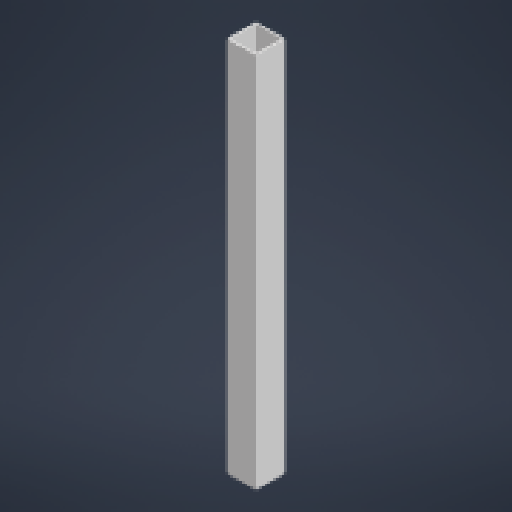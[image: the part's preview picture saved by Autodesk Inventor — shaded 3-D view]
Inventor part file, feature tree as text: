
AUTODESK INVENTOR PART (.ipt)
format: ipt  version: 2024 (Build 280153000, 153)  size: 129,536 bytes
history: native  units: in
note: dims shown in document units (in); Inventor stores cm internally (conversion verified against a paired STEP export)
features: plane x1, extrude x1, sketch x1
ambient origin geometry x8: Origin, YZ Plane, XZ Plane, XY Plane, X Axis, Y Axis, Z Axis, Center Point
bodies: Solid1 (feature_tree)
feature tree (3):
  plane  "Work Plane1"
  extrude  "Extrusion1"  Depth=1.0in
  sketch  "Sketch1"  dims[d0=1.0in d1=1.0in d2=0.0625in d3=0.0625in d4=0.0625in d5=0.0625in d6=13.0in d7=0.0in]
